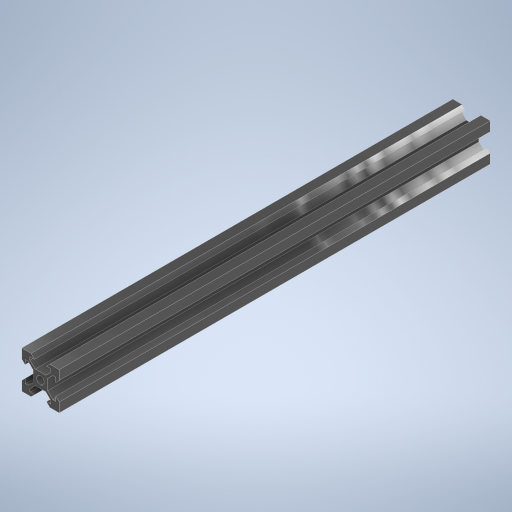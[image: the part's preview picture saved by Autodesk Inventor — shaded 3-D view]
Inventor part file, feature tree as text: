
AUTODESK INVENTOR PART (.ipt)
format: ipt  version: 2024.2 (Build 282272000, 272)  size: 316,928 bytes
history: native  units: mm
features: extrude x1, sketch x1
ambient origin geometry x8: Origin, YZ Plane, XZ Plane, XY Plane, X Axis, Y Axis, Z Axis, Center Point
bodies: Solid1 (feature_tree)
feature tree (2):
  extrude  "Extrusion1"  Depth=230.0mm
  sketch  "Sketch1"  dims[d16=10.0mm d19=3.2mm d21=4.4mm d22=4.4mm d24=45.0deg d25=1.8mm d27=1.8mm d28=45.0deg d29=3.2mm d31=1.4mm d33=2.15mm d34=3.825mm d35=3.825mm d36=135.0deg d37=40.0mm d39=360.0deg d41=230.0mm d42=0.0mm]
